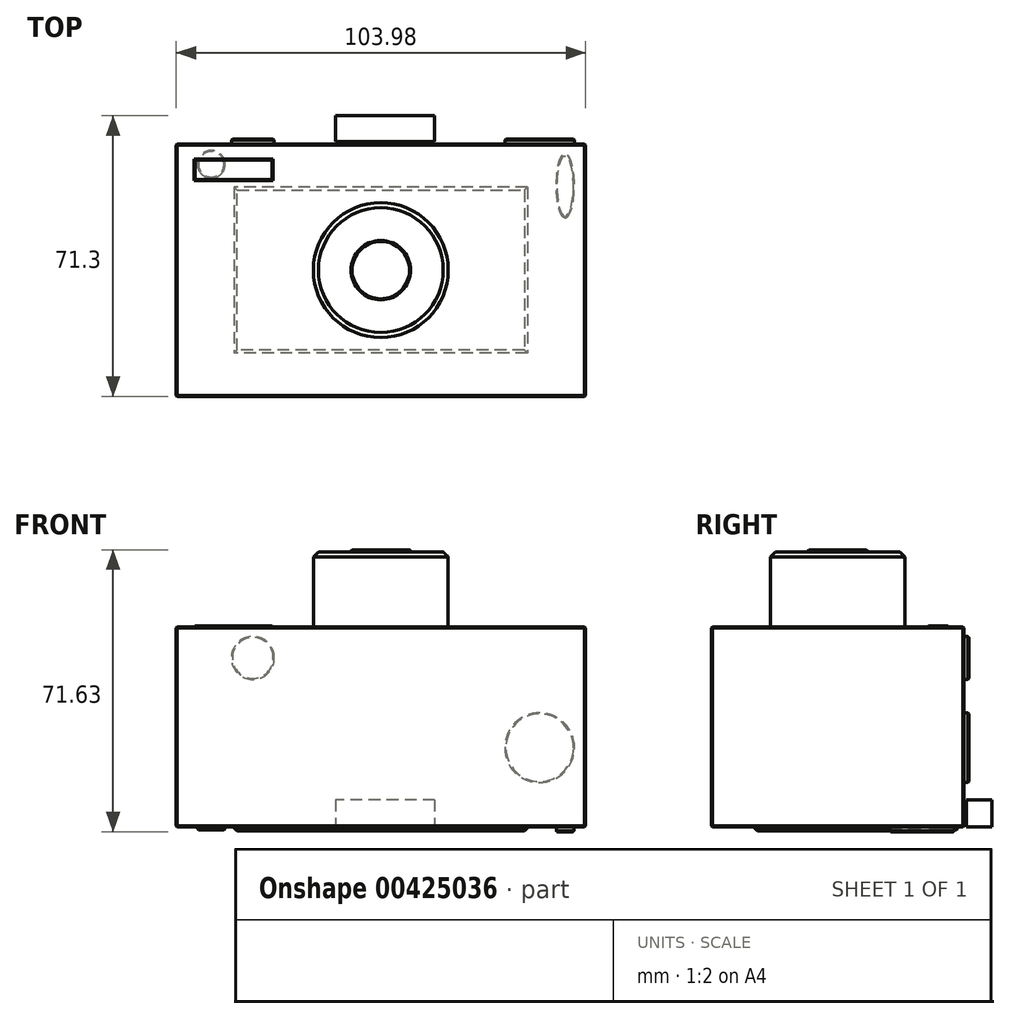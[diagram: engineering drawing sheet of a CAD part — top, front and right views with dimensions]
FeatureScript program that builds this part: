
annotation { "Feature Type Name" : "Feature", "Feature Type Description" : "" }
export const myFeature = defineFeature(function(context is Context, id is Id, definition is map)
    precondition{}
    {
        {
            var Q0;
            Q0=qCreatedBy(makeId("Top.planeOp"),FACE);
            var sketch = newSketch(context, id + "F0", { "sketchPlane" : qUnion([Q0])});
            skLineSegment(sketch, "E0.bottom", {"start": v(-52, 32.07) * mm, "end": v(52, 32.07) * mm});
            skLineSegment(sketch, "E0.top", {"start": v(-52, -32.07) * mm, "end": v(52, -32.07) * mm});
            skLineSegment(sketch, "E0.left", {"start": v(-52, 32.07) * mm, "end": v(-52, -32.07) * mm});
            skLineSegment(sketch, "E0.right", {"start": v(52, 32.07) * mm, "end": v(52, -32.07) * mm});
            skPoint(sketch, "E0.middle", {"position": v(0, 0) * mm});
            skSolve(sketch);
        }
        {
            var Q0;
            Q0=makeQuery(id+"F0.imprint","IMPRINT",FACE,{"disambiguationData":[TD([[makeQuery(id+"F0.imprint","IMPRINT",EDGE,{"derivedFrom":sQuery(id+"F0.wireOp",EDGE,"E0.bottom")}),-1.0]])]});
            extrude(context, id + "F1", {"entities" : qUnion([Q0]), "depth" : 50.8 * mm});
        }
        {
            var Q0;
            Q0=makeQuery(id+"F1.opExtrude","CAP_FACE",FACE,{"disambiguationData":[OSD([sQuery(id+"F0.wireOp",EDGE,"E0.bottom"),sQuery(id+"F0.wireOp",EDGE,"E0.top"),sQuery(id+"F0.wireOp",EDGE,"E0.left"),sQuery(id+"F0.wireOp",EDGE,"E0.right")])],"isStart":false});
            var sketch = newSketch(context, id + "F2", { "sketchPlane" : qUnion([Q0])});
            skCircle(sketch, "E1", {"center": v(0, 0) * mm, "radius": 17.12 * mm});
            skSolve(sketch);
        }
        {
            var Q0;
            Q0=makeQuery(id+"F2.imprint","IMPRINT",FACE,{"disambiguationData":[TD([[makeQuery(id+"F2.imprint","IMPRINT",EDGE,{"derivedFrom":sQuery(id+"F2.wireOp",EDGE,"E1")}),1.0]])]});
            extrude(context, id + "F3", {"entities" : qUnion([Q0]), "operationType" : NewBodyOperationType.ADD, "depth" : 19.05 * mm});
        }
        {
            var Q0;
            Q0=makeQuery(id+"F3.opExtrude","CAP_FACE",FACE,{"disambiguationData":[OSD([sQuery(id+"F2.wireOp",EDGE,"E1")])],"isStart":false});
            var sketch = newSketch(context, id + "F4", { "sketchPlane" : qUnion([Q0])});
            skCircle(sketch, "E2", {"center": v(0, 0) * mm, "radius": 7.54 * mm});
            skSolve(sketch);
        }
        {
            var Q0;
            Q0=makeQuery(id+"F4.imprint","IMPRINT",FACE,{"disambiguationData":[TD([[makeQuery(id+"F4.imprint","IMPRINT",EDGE,{"derivedFrom":sQuery(id+"F4.wireOp",EDGE,"E2")}),1.0]])]});
            extrude(context, id + "F5", {"entities" : qUnion([Q0]), "operationType" : NewBodyOperationType.ADD, "depth" : 0.5 * mm});
        }
        {
            var Q0;
            Q0=makeQuery(id+"F1.opExtrude","SWEPT_FACE",FACE,{"disambiguationData":[OSD([sQuery(id+"F0.wireOp",EDGE,"E0.bottom")])]});
            var sketch = newSketch(context, id + "F6", { "sketchPlane" : qUnion([Q0])});
            skCircle(sketch, "E3", {"center": v(32.51, 42.9) * mm, "radius": 5.46 * mm});
            skSolve(sketch);
        }
        {
            var Q0;
            Q0=makeQuery(id+"F6.imprint","IMPRINT",FACE,{"disambiguationData":[TD([[makeQuery(id+"F6.imprint","IMPRINT",EDGE,{"derivedFrom":sQuery(id+"F6.wireOp",EDGE,"E3")}),1.0]])]});
            var Q1;
            Q1 = qSketchRegion(id + "F16", true);
            extrude(context, id + "F7", {"entities" : qUnion([Q0, Q1]), "depth" : 1.27 * mm});
        }
        {
            var Q0;
            Q0=makeQuery(id+"F1.opExtrude","CAP_FACE",FACE,{"disambiguationData":[OSD([sQuery(id+"F0.wireOp",EDGE,"E0.bottom"),sQuery(id+"F0.wireOp",EDGE,"E0.top"),sQuery(id+"F0.wireOp",EDGE,"E0.left"),sQuery(id+"F0.wireOp",EDGE,"E0.right")])],"isStart":true});
            var sketch = newSketch(context, id + "F8", { "sketchPlane" : qUnion([Q0])});
            skLineSegment(sketch, "E4.bottom", {"start": v(37.28, -21.1) * mm, "end": v(-37.28, -21.1) * mm});
            skLineSegment(sketch, "E4.top", {"start": v(37.28, 21.1) * mm, "end": v(-37.28, 21.1) * mm});
            skLineSegment(sketch, "E4.left", {"start": v(37.28, -21.1) * mm, "end": v(37.28, 21.1) * mm});
            skLineSegment(sketch, "E4.right", {"start": v(-37.28, -21.1) * mm, "end": v(-37.28, 21.1) * mm});
            skPoint(sketch, "E4.middle", {"position": v(0, 0) * mm});
            skSolve(sketch);
        }
        {
            var Q0;
            Q0=makeQuery(id+"F8.imprint","IMPRINT",FACE,{"disambiguationData":[TD([[makeQuery(id+"F8.imprint","IMPRINT",EDGE,{"derivedFrom":sQuery(id+"F8.wireOp",EDGE,"E4.bottom")}),-1.0]])]});
            extrude(context, id + "F9", {"entities" : qUnion([Q0]), "operationType" : NewBodyOperationType.ADD, "depth" : 1.02 * mm});
        }
        {
            var Q0;
            Q0=makeQuery(id+"F1.opExtrude","CAP_FACE",FACE,{"disambiguationData":[OSD([sQuery(id+"F0.wireOp",EDGE,"E0.bottom"),sQuery(id+"F0.wireOp",EDGE,"E0.top"),sQuery(id+"F0.wireOp",EDGE,"E0.left"),sQuery(id+"F0.wireOp",EDGE,"E0.right")])],"isStart":false});
            var sketch = newSketch(context, id + "F10", { "sketchPlane" : qUnion([Q0])});
            skLineSegment(sketch, "E5.bottom", {"start": v(-47.5, 28.26) * mm, "end": v(-27.4, 28.26) * mm});
            skLineSegment(sketch, "E5.top", {"start": v(-47.5, 22.81) * mm, "end": v(-27.4, 22.81) * mm});
            skLineSegment(sketch, "E5.left", {"start": v(-47.5, 28.26) * mm, "end": v(-47.5, 22.81) * mm});
            skLineSegment(sketch, "E5.right", {"start": v(-27.4, 28.26) * mm, "end": v(-27.4, 22.81) * mm});
            skSolve(sketch);
        }
        {
            var Q0;
            Q0=makeQuery(id+"F10.imprint","IMPRINT",FACE,{"disambiguationData":[TD([[makeQuery(id+"F10.imprint","IMPRINT",EDGE,{"derivedFrom":sQuery(id+"F10.wireOp",EDGE,"E5.bottom")}),-1.0]])]});
            extrude(context, id + "F11", {"entities" : qUnion([Q0]), "operationType" : NewBodyOperationType.ADD, "depth" : 0.25 * mm});
        }
        {
            var Q0;
            Q0=makeQuery(id+"F1.opExtrude","CAP_FACE",FACE,{"disambiguationData":[OSD([sQuery(id+"F0.wireOp",EDGE,"E0.bottom"),sQuery(id+"F0.wireOp",EDGE,"E0.top"),sQuery(id+"F0.wireOp",EDGE,"E0.left"),sQuery(id+"F0.wireOp",EDGE,"E0.right")])],"isStart":true});
            var sketch = newSketch(context, id + "F12", { "sketchPlane" : qUnion([Q0])});
            skEllipse(sketch, "E6", {"center": v(46.81, -21.45) * mm, "majorRadius": 8.17 * mm, "minorRadius": 2.23 * mm, "majorAxis": v(0, 1)});
            skSolve(sketch);
        }
        {
            var Q0;
            Q0=makeQuery(id+"F12.imprint","IMPRINT",FACE,{"disambiguationData":[TD([[makeQuery(id+"F12.imprint","IMPRINT",EDGE,{"derivedFrom":sQuery(id+"F12.wireOp",EDGE,"E6")}),1.0]])]});
            extrude(context, id + "F13", {"entities" : qUnion([Q0]), "operationType" : NewBodyOperationType.ADD, "depth" : 1.27 * mm});
        }
        {
            var Q0;
            Q0=makeQuery(id+"F1.opExtrude","CAP_FACE",FACE,{"disambiguationData":[OSD([sQuery(id+"F0.wireOp",EDGE,"E0.bottom"),sQuery(id+"F0.wireOp",EDGE,"E0.top"),sQuery(id+"F0.wireOp",EDGE,"E0.left"),sQuery(id+"F0.wireOp",EDGE,"E0.right")])],"isStart":true});
            var sketch = newSketch(context, id + "F14", { "sketchPlane" : qUnion([Q0])});
            skCircle(sketch, "E7", {"center": v(-43.07, -26.9) * mm, "radius": 3.5 * mm});
            skSolve(sketch);
        }
        {
            var Q0;
            Q0=makeQuery(id+"F14.imprint","IMPRINT",FACE,{"disambiguationData":[TD([[makeQuery(id+"F14.imprint","IMPRINT",EDGE,{"derivedFrom":sQuery(id+"F14.wireOp",EDGE,"E7")}),1.0]])]});
            extrude(context, id + "F15", {"entities" : qUnion([Q0]), "operationType" : NewBodyOperationType.ADD, "depth" : 0.76 * mm});
        }
        {
            var Q0;
            Q0=makeQuery(id+"F1.opExtrude","SWEPT_FACE",FACE,{"disambiguationData":[OSD([sQuery(id+"F0.wireOp",EDGE,"E0.bottom")])]});
            var sketch = newSketch(context, id + "F16", { "sketchPlane" : qUnion([Q0])});
            skCircle(sketch, "E8", {"center": v(-40.35, 20.09) * mm, "radius": 8.85 * mm});
            skSolve(sketch);
        }
        {
            var Q0;
            Q0=makeQuery(id+"F16.imprint","IMPRINT",FACE,{"disambiguationData":[TD([[makeQuery(id+"F16.imprint","IMPRINT",EDGE,{"derivedFrom":sQuery(id+"F16.wireOp",EDGE,"E8")}),1.0]])]});
            extrude(context, id + "F17", {"entities" : qUnion([Q0]), "operationType" : NewBodyOperationType.ADD, "depth" : 1.27 * mm});
        }
        {
            var Q0;
            Q0=makeQuery(id+"F1.opExtrude","CAP_EDGE",EDGE,{"disambiguationData":[OSD([sQuery(id+"F0.wireOp",EDGE,"E0.bottom")])],"isStart":false});
            chamfer(context, id + "F18", {"entities" : qUnion([Q0]), "width" : 0.25 * mm, "tangentPropagation" : true});
        }
        {
            var Q0;
            Q0=makeQuery(id+"F1.opExtrude","CAP_EDGE",EDGE,{"disambiguationData":[OSD([sQuery(id+"F0.wireOp",EDGE,"E0.top")])],"isStart":false});
            chamfer(context, id + "F19", {"entities" : qUnion([Q0]), "width" : 0.25 * mm, "tangentPropagation" : true});
        }
        {
            var Q0;
            Q0=makeQuery(id+"F1.opExtrude","CAP_EDGE",EDGE,{"disambiguationData":[OSD([sQuery(id+"F0.wireOp",EDGE,"E0.left")])],"isStart":false});
            chamfer(context, id + "F20", {"entities" : qUnion([Q0]), "width" : 0.25 * mm, "tangentPropagation" : true});
        }
        {
            var Q0;
            Q0=makeQuery(id+"F1.opExtrude","CAP_EDGE",EDGE,{"disambiguationData":[OSD([sQuery(id+"F0.wireOp",EDGE,"E0.right")])],"isStart":false});
            chamfer(context, id + "F21", {"entities" : qUnion([Q0]), "width" : 0.25 * mm, "tangentPropagation" : true});
        }
        {
            var Q0;
            Q0=makeQuery(id+"F1.opExtrude","CAP_EDGE",EDGE,{"disambiguationData":[OSD([sQuery(id+"F0.wireOp",EDGE,"E0.bottom")])],"isStart":true});
            chamfer(context, id + "F22", {"entities" : qUnion([Q0]), "width" : 0.25 * mm, "tangentPropagation" : true});
        }
        {
            var Q0;
            Q0=makeQuery(id+"F1.opExtrude","CAP_EDGE",EDGE,{"disambiguationData":[OSD([sQuery(id+"F0.wireOp",EDGE,"E0.right")])],"isStart":true});
            chamfer(context, id + "F23", {"entities" : qUnion([Q0]), "width" : 0.25 * mm, "tangentPropagation" : true});
        }
        {
            var Q0;
            Q0=makeQuery(id+"F1.opExtrude","CAP_EDGE",EDGE,{"disambiguationData":[OSD([sQuery(id+"F0.wireOp",EDGE,"E0.top")])],"isStart":true});
            chamfer(context, id + "F24", {"entities" : qUnion([Q0]), "width" : 0.25 * mm, "tangentPropagation" : true});
        }
        {
            var Q0;
            Q0=makeQuery(id+"F1.opExtrude","CAP_EDGE",EDGE,{"disambiguationData":[OSD([sQuery(id+"F0.wireOp",EDGE,"E0.left")])],"isStart":true});
            chamfer(context, id + "F25", {"entities" : qUnion([Q0]), "width" : 0.25 * mm, "tangentPropagation" : true});
        }
        {
            var Q0;
            Q0=makeQuery(id+"F1.opExtrude","SWEPT_EDGE",EDGE,{"disambiguationData":[OSD([sQuery(id+"F0.wireOp",EDGE,"E0.bottom"),sQuery(id+"F0.wireOp",EDGE,"E0.right")])]});
            chamfer(context, id + "F26", {"entities" : qUnion([Q0]), "width" : 0.25 * mm, "tangentPropagation" : true});
        }
        {
            var Q0;
            Q0=makeQuery(id+"F1.opExtrude","SWEPT_EDGE",EDGE,{"disambiguationData":[OSD([sQuery(id+"F0.wireOp",EDGE,"E0.bottom"),sQuery(id+"F0.wireOp",EDGE,"E0.left")])]});
            chamfer(context, id + "F27", {"entities" : qUnion([Q0]), "width" : 0.25 * mm, "tangentPropagation" : true});
        }
        {
            var Q0;
            Q0=makeQuery(id+"F1.opExtrude","SWEPT_EDGE",EDGE,{"disambiguationData":[OSD([sQuery(id+"F0.wireOp",EDGE,"E0.top"),sQuery(id+"F0.wireOp",EDGE,"E0.right")])]});
            chamfer(context, id + "F28", {"entities" : qUnion([Q0]), "width" : 0.25 * mm, "tangentPropagation" : true});
        }
        {
            var Q0;
            Q0=makeQuery(id+"F1.opExtrude","SWEPT_EDGE",EDGE,{"disambiguationData":[OSD([sQuery(id+"F0.wireOp",EDGE,"E0.top"),sQuery(id+"F0.wireOp",EDGE,"E0.left")])]});
            chamfer(context, id + "F29", {"entities" : qUnion([Q0]), "width" : 0.25 * mm, "tangentPropagation" : true});
        }
        {
            var Q0;
            Q0=makeQuery(id+"F3.opExtrude","CAP_EDGE",EDGE,{"disambiguationData":[OSD([sQuery(id+"F2.wireOp",EDGE,"E1")])],"isStart":false});
            chamfer(context, id + "F30", {"entities" : qUnion([Q0]), "width" : 1.27 * mm, "tangentPropagation" : true});
        }
        {
            var Q0;
            Q0=makeQuery(id+"F5.opExtrude","CAP_FACE",FACE,{"disambiguationData":[OSD([sQuery(id+"F4.wireOp",EDGE,"E2")])],"isStart":false});
            chamfer(context, id + "F31", {"entities" : qUnion([Q0]), "width" : 0.25 * mm, "tangentPropagation" : true});
        }
        {
            var Q0;
            Q0=makeQuery(id+"F9.opExtrude","CAP_FACE",FACE,{"disambiguationData":[OSD([sQuery(id+"F8.wireOp",EDGE,"E4.bottom"),sQuery(id+"F8.wireOp",EDGE,"E4.top"),sQuery(id+"F8.wireOp",EDGE,"E4.left"),sQuery(id+"F8.wireOp",EDGE,"E4.right")])],"isStart":false});
            chamfer(context, id + "F32", {"entities" : qUnion([Q0]), "width" : 0.76 * mm, "tangentPropagation" : true});
        }
        {
            var Q0;
            Q0=makeQuery(id+"F13.opExtrude","CAP_EDGE",EDGE,{"disambiguationData":[OSD([sQuery(id+"F12.wireOp",EDGE,"E6")])],"isStart":false});
            chamfer(context, id + "F33", {"entities" : qUnion([Q0]), "width" : 0.25 * mm, "tangentPropagation" : true});
        }
        {
            var Q0;
            Q0=makeQuery(id+"F15.opExtrude","CAP_EDGE",EDGE,{"disambiguationData":[OSD([sQuery(id+"F14.wireOp",EDGE,"E7")])],"isStart":false});
            chamfer(context, id + "F34", {"entities" : qUnion([Q0]), "width" : 0.25 * mm, "tangentPropagation" : true});
        }
        {
            var Q0;
            Q0=makeQuery(id+"F7.opExtrude","CAP_FACE",FACE,{"disambiguationData":[OSD([sQuery(id+"F6.wireOp",EDGE,"E3")])],"isStart":false});
            chamfer(context, id + "F35", {"entities" : qUnion([Q0]), "width" : 0.25 * mm, "tangentPropagation" : true});
        }
        {
            var Q0;
            Q0=makeQuery(id+"F17.opExtrude","CAP_EDGE",EDGE,{"disambiguationData":[OSD([sQuery(id+"F16.wireOp",EDGE,"E8")])],"isStart":false});
            chamfer(context, id + "F36", {"entities" : qUnion([Q0]), "width" : 0.25 * mm, "tangentPropagation" : true});
        }
        {
            var Q0;
            Q0=makeQuery(id+"F11.opExtrude","CAP_FACE",FACE,{"disambiguationData":[OSD([sQuery(id+"F10.wireOp",EDGE,"E5.bottom"),sQuery(id+"F10.wireOp",EDGE,"E5.top"),sQuery(id+"F10.wireOp",EDGE,"E5.left"),sQuery(id+"F10.wireOp",EDGE,"E5.right")])],"isStart":false});
            chamfer(context, id + "F37", {"entities" : qUnion([Q0]), "width" : 0.25 * mm, "tangentPropagation" : true});
        }
        {
            var Q0;
            Q0=qCreatedBy(makeId("Top.planeOp"),FACE);
            var sketch = newSketch(context, id + "F38", { "sketchPlane" : qUnion([Q0])});
            skLineSegment(sketch, "E9.bottom", {"start": v(13.7, 32.69) * mm, "end": v(-11.52, 32.69) * mm});
            skLineSegment(sketch, "E9.top", {"start": v(13.7, 39.23) * mm, "end": v(-11.52, 39.23) * mm});
            skLineSegment(sketch, "E9.left", {"start": v(13.7, 32.69) * mm, "end": v(13.7, 39.23) * mm});
            skLineSegment(sketch, "E9.right", {"start": v(-11.52, 32.69) * mm, "end": v(-11.52, 39.23) * mm});
            skSolve(sketch);
        }
        {
            var Q0;
            Q0=makeQuery(id+"F38.imprint","IMPRINT",FACE,{"disambiguationData":[TD([[makeQuery(id+"F38.imprint","IMPRINT",EDGE,{"derivedFrom":sQuery(id+"F38.wireOp",EDGE,"E9.bottom")}),-1.0]])]});
            extrude(context, id + "F39", {"entities" : qUnion([Q0]), "depth" : 6.86 * mm});
        }
    });
